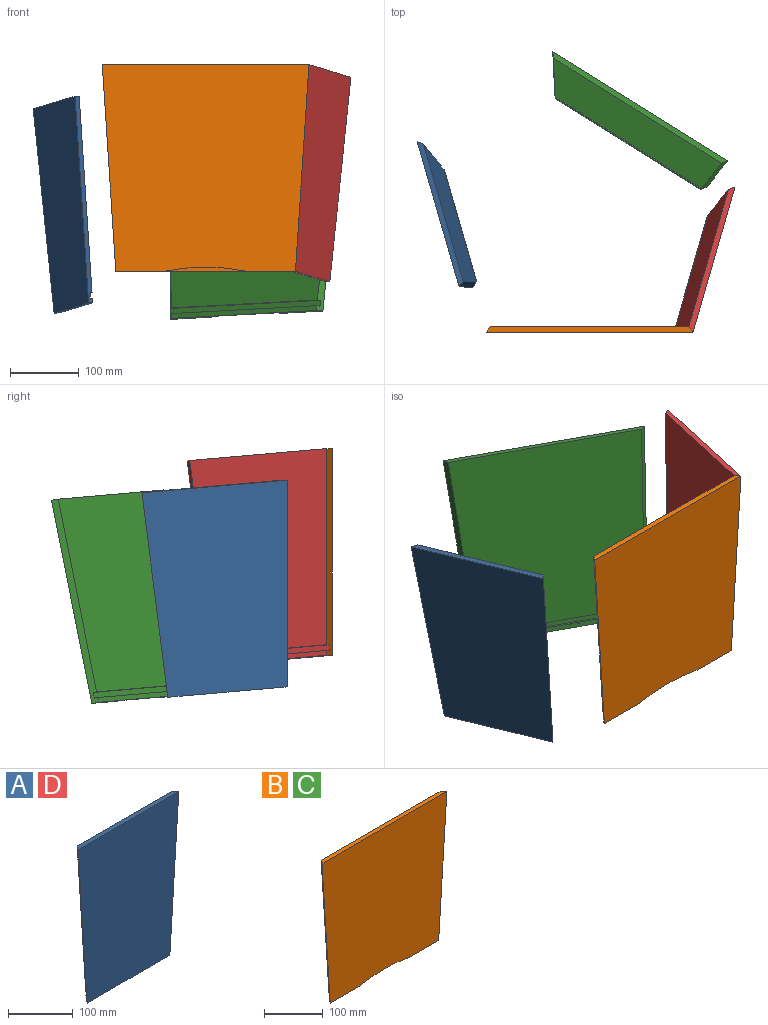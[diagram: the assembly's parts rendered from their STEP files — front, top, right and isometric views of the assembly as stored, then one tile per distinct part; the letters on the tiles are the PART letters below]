
ASSEMBLY  parts=4 mates=1
PART A: 11 faces, bbox 220x8x300 mm
  f0: plane 169.61x7mm, normal (0,1,0), area 1184.1mm2, adj f1,f2,f3,f9
  f1: plane 300x25.65mm, normal (-0.8,0.6,-0.05), area 2962.1mm2, adj f0,f3,f4,f5,f6,f8,f9,f10
  f2: plane 300x25.65mm, normal (0.8,0.6,-0.05), area 2962.1mm2, adj f0,f3,f4,f5,f6,f8,f9,f10
  f3: plane 180.7x8.01mm, normal (0,0,-1), area 1383.8mm2, adj f0,f1,f2,f6,f7
  f4: plane 220x8mm, normal (0,0,1), area 1712mm2, adj f1,f2,f5,f6
  f5: plane 284.6x208mm, normal (0,1,0), area 53890.7mm2, adj f1,f2,f4,f8
  f6: plane 300x220mm, normal (0,-1,0), area 60104.1mm2, adj f1,f2,f3,f4,f7
  f7: cylinder r=180mm len=6mm, axis (0,-1,0), area 13.8mm2, adj f3,f6
  f8: plane 176.71x4mm, normal (0,0,-1), area 694.8mm2, adj f1,f2,f5,f10
  f9: plane 175.61x4mm, normal (0,0,1), area 690.4mm2, adj f0,f1,f2,f10
  f10: plane 176.71x8.4mm, normal (0,1,0), area 1479.8mm2, adj f1,f2,f8,f9
PART B: 12 faces, bbox 300x8x300 mm
  f0: plane 249.61x7mm, normal (0,1,0), area 1744.1mm2, adj f2,f5,f6,f9
  f1: plane 288x284.62mm, normal (0,1,0), area 76664.5mm2, adj f3,f5,f6,f10
  f2: plane 260.69x8mm, normal (0,0,-1), area 1317.6mm2, adj f0,f4,f5,f6,f7,f8
  f3: plane 300x8mm, normal (0,0,1), area 2352mm2, adj f1,f4,f5,f6
  f4: plane 300x300mm, normal (0,-1,0), area 83618.2mm2, adj f2,f3,f5,f6,f7
  f5: plane 300x25.65mm, normal (-0.8,0.6,-0.05), area 2962.2mm2, adj f0,f1,f2,f3,f4,f9,f10,f11
  f6: plane 300x25.65mm, normal (0.8,0.6,-0.05), area 2962.2mm2, adj f0,f1,f2,f3,f4,f9,f10,f11
  f7: cylinder r=300mm len=120mm, axis (0,-1,0), area 724.9mm2, adj f2,f4,f8
  f8: plane 120x6.06mm, normal (0,-1,0), area 485.9mm2, adj f2,f7
  f9: plane 255.61x4mm, normal (0,0,1), area 1010.4mm2, adj f0,f5,f6,f11
  f10: plane 256.71x4mm, normal (0,0,-1), area 1014.8mm2, adj f1,f5,f6,f11
  f11: plane 256.71x8.38mm, normal (0,1,0), area 2145.9mm2, adj f5,f6,f9,f10
PART C: same geometry as B
PART D: same geometry as A
PLACE A rot(axis=(0,-0.09,-1),73.9deg) t=(-60.15,-352.06,402.96)mm
PLACE B t=(7.45,-604.02,465.06)mm
PLACE C rot(axis=(0,0.09,1),147.9deg) t=(339.98,-417.87,409.44)mm
PLACE D rot(axis=(0,0.09,1),73.9deg) t=(274.7,-628.58,467.21)mm
MATE slider D.f1 <-> B.f6  axis (-0.8,-0.6,0.05) through (304.45,-608.02,765.06)mm
